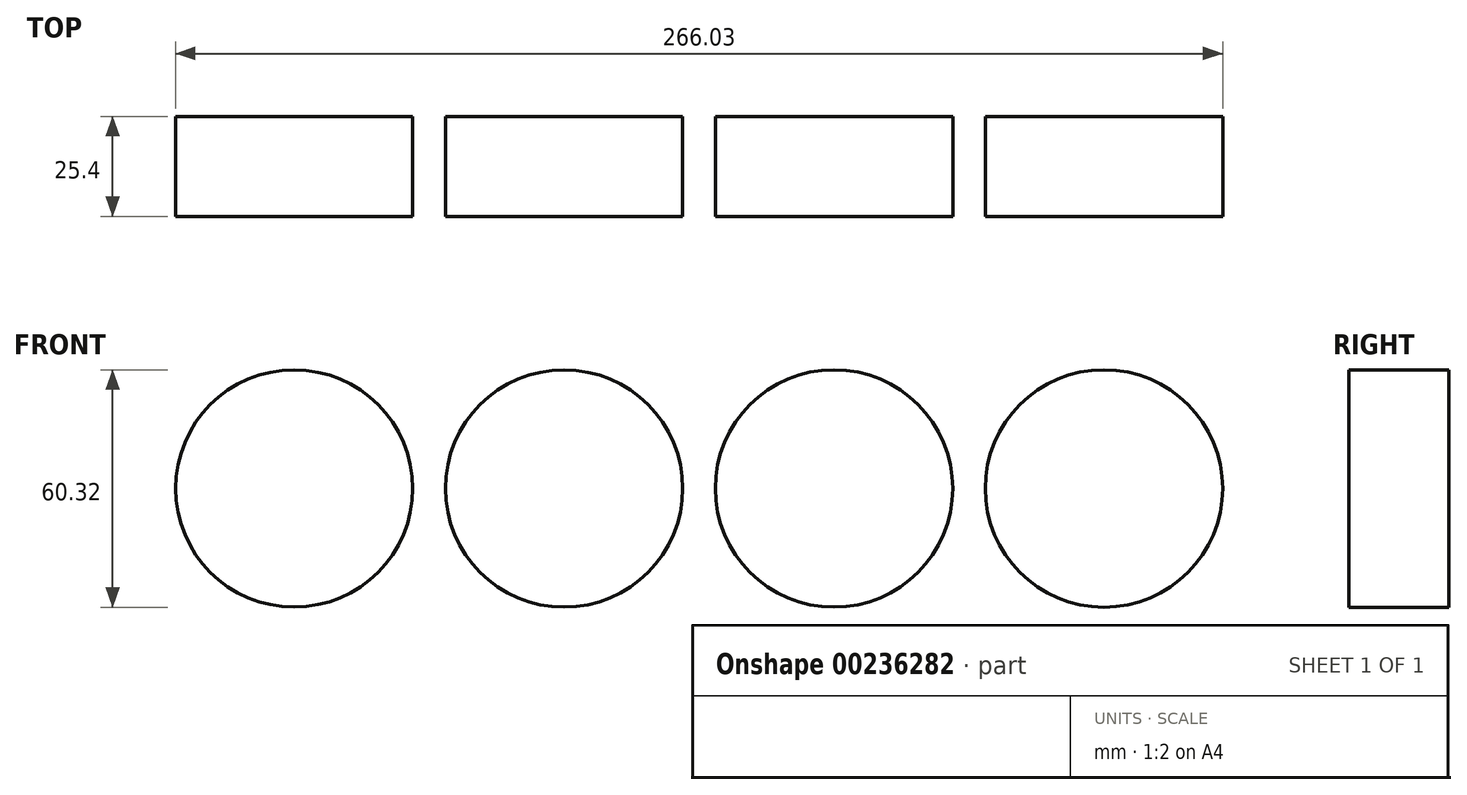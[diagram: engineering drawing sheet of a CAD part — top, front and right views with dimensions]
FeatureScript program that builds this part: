
annotation { "Feature Type Name" : "Feature", "Feature Type Description" : "" }
export const myFeature = defineFeature(function(context is Context, id is Id, definition is map)
    precondition{}
    {
        {
            var Q0;
            Q0=qCreatedBy(makeId("Front.planeOp"),FACE);
            var sketch = newSketch(context, id + "F0", { "sketchPlane" : qUnion([Q0])});
            skCircle(sketch, "E0", {"center": v(-85.72, 0) * mm, "radius": 30.12 * mm});
            skCircle(sketch, "E1", {"center": v(-17.14, 0) * mm, "radius": 30.14 * mm});
            skCircle(sketch, "E2", {"center": v(51.44, 0) * mm, "radius": 30.15 * mm});
            skCircle(sketch, "E3", {"center": v(120.02, 0) * mm, "radius": 30.16 * mm});
            skSolve(sketch);
        }
        {
            var Q0;
            Q0=makeQuery(id+"F0.imprint","IMPRINT",FACE,{"disambiguationData":[TD([[makeQuery(id+"F0.imprint","IMPRINT",EDGE,{"derivedFrom":sQuery(id+"F0.wireOp",EDGE,"E0")}),1.0]])]});
            var Q1;
            Q1=makeQuery(id+"F0.imprint","IMPRINT",FACE,{"disambiguationData":[TD([[makeQuery(id+"F0.imprint","IMPRINT",EDGE,{"derivedFrom":sQuery(id+"F0.wireOp",EDGE,"E1")}),1.0]])]});
            var Q2;
            Q2=makeQuery(id+"F0.imprint","IMPRINT",FACE,{"disambiguationData":[TD([[makeQuery(id+"F0.imprint","IMPRINT",EDGE,{"derivedFrom":sQuery(id+"F0.wireOp",EDGE,"E2")}),1.0]])]});
            var Q3;
            Q3=makeQuery(id+"F0.imprint","IMPRINT",FACE,{"disambiguationData":[TD([[makeQuery(id+"F0.imprint","IMPRINT",EDGE,{"derivedFrom":sQuery(id+"F0.wireOp",EDGE,"E3")}),1.0]])]});
            extrude(context, id + "F1", {"entities" : qUnion([Q0, Q1, Q2, Q3]), "depth" : 25.4 * mm});
        }
    });
